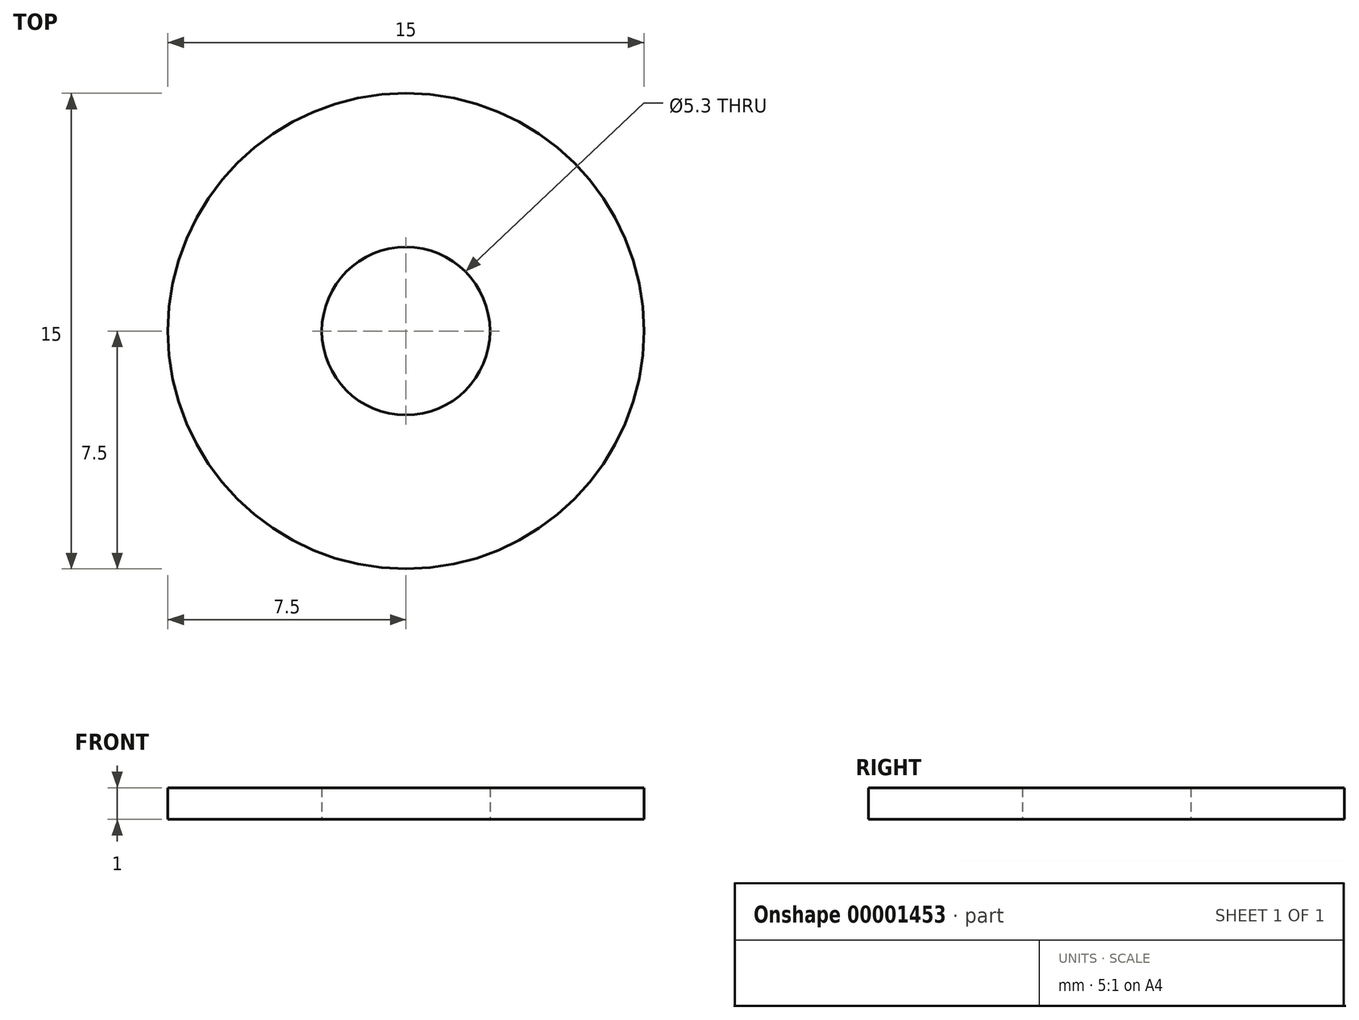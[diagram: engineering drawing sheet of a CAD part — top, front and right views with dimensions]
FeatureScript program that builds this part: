
annotation { "Feature Type Name" : "Feature", "Feature Type Description" : "" }
export const myFeature = defineFeature(function(context is Context, id is Id, definition is map)
    precondition{}
    {
        {
            var Q0;
            Q0=qCreatedBy(makeId("Top.planeOp"),FACE);
            var sketch = newSketch(context, id + "F0", { "sketchPlane" : qUnion([Q0])});
            skCircle(sketch, "E0", {"center": v(0, 0) * mm, "radius": 7.5 * mm});
            skCircle(sketch, "E1", {"center": v(0, 0) * mm, "radius": 2.65 * mm});
            skSolve(sketch);
        }
        {
            var Q0;
            Q0=makeQuery(id+"F0.imprint","IMPRINT",FACE,{"disambiguationData":[TD([[makeQuery(id+"F0.imprint","IMPRINT",EDGE,{"derivedFrom":sQuery(id+"F0.wireOp",EDGE,"E0")}),1.0]])]});
            extrude(context, id + "F1", {"entities" : qUnion([Q0]), "depth" : 1 * mm});
        }
    });
